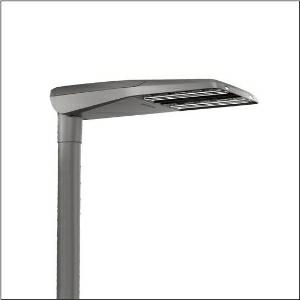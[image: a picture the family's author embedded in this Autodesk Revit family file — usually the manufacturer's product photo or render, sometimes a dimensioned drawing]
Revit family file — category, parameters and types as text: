
# Revit family: streetlight_sl_11_iq_midi___st1_2a_5xc3a21f08me_5047
name_source: partatom
category: Lighting Fixtures
units: mm (PartAtom-declared; Revit-internal decimal feet)

## family parameters
Cut with Voids When Loaded = No
Host = Face
Light Source = No
Part Type = Normal
Room Calculation Point = No
Round Connector Dimension = Use Diameter
Shared = No

## types (1)
- --- (1 x LED, 14840 lm, 124.7 W, 2200K)
    Apparent Load = 125 VA
    CIE Flux Codes = 32 70 96 100 100
    Color Rendering = 70
    Color Temperature = 2200K
    Default Elevation = 1800 mm
    Description = Streetlight SL 11 iQ midi, mast luminaire, primary light control with 3 zone facetted reflector, of plastic, silver coated, highly specular, primary optical cover: cover, of PMMA, transparent, light distribution: ST1.2a, light emission: direct distribution, primary light characteristic: asymmetric, installation type: post-top, side-entry, lamps: LED, High Power LED, rated values: 14.840lm | 124,7W | 119lm/W (begin service life); end service life: 14.840lm | 132,2W; at 50% lumin. flux: 7.420lm | 57,1W | 129,9lm/W, colour temperature: 2200K, colour rendering: CRI > 70, light colour: 722, light setting 1 begin service life: 100% | 14.840lm | 124,7W | 119lm/W | 2.200K, light setting 1 end service life: 132,2W, further light settings possible, control: Street-Remote, optimised constant luminous flux control (CLO 2.0), Desk-Remote (wireless, voltage-free reading and setting of iQ features in the workshop via application-optimized NFC function/RFID function), Light-Fading, Smart-Wire, Night-Set, Lumen-Switch, Temp-Guard, Auto-Match, with cable H07RN-F 5x 1.5mm², mains connection: 230..240V, AC, 50/60Hz, connection cable pre-assembled, cable length: 12,5m, luminaire housing, of diecast aluminium, powder-coated, Siteco® metallic grey (DB 702S), please order mast flange separately, inclination adjustable without tools: 0°, 5°, 10°, 15° (post-top) | 0°, -5°, -10°, -15° (side-entry), sealing non-destructively replaceable, multi-level sealing system, length: 780mm, width: 376mm, height: 118mm, mast flange for spigot size: 42mm (side-entry): 5XC10008XM4, 60/48mm (side-entry/post-top): 5XC10108XM2, 76/60mm (side-entry/post-top): 5XC10108XM1, equipment: Power, protection rating (complete): IP66, insulation class (complete): insulation class II (safety insulation), certification: CE, ENEC, ENEC+, VDE, impact resistance: IK10, permissible operating ambient temperature for outdoor applications: -25..+50°C, standard-compliant lighting for roads and squares, Environmental Product Declaration (EPD) tested and certified by an independent institute, packaging unit: 1 piece

Light Distribution: ST1.2a
    Height = 118 mm
    Lamp = 1 x LED
    Lamp Light Flux = 14840 lm
    Lamp Power = 124.7 W
    Lamp count = 1
    Length = 780 mm
    Luminous efficacy = 119 lm/W
    Manufacturer = Siteco
    ModVariant = No
    Model = 5XC3A21F08ME
    Number of Poles = 1
    OnlyDefault = Yes
    Power Factor = 1
    Product Name = Streetlight SL 11 iQ midi | ST1.2a
    Product group = mast luminaire | pylon top
    ProductGroupID = 6100
    Protection Class = Protection class II
    Protection Degree = IP 66
    RLX_Detail_Level = 1
    RLX_Emergency_Light_Flux = 0 lm
    RLX_Emergency_Type = 0
    RLX_Emergency_Type_DB = No
    RlxData = <blob elided: 70925 chars, md5=a2024761>
    Socket = socket
    Standby Power = 0 W
    System Light Flux = 14841 lm
    System Power = 125 W
    Type Comments = factory setting: luminous flux: 100 % | dim-lin: 254 | 557 mA
    Type Image = l_1005960.jpg
    URL = http://relux.com
    VarID = @adj_150949
    Voltage = 0 V
    Weight = 0.00 kg
    Width = 376 mm

## geometry (parser evidence)
native form markers: Blend x4, Sweep x11
no freeform markers — native parametric forms only
